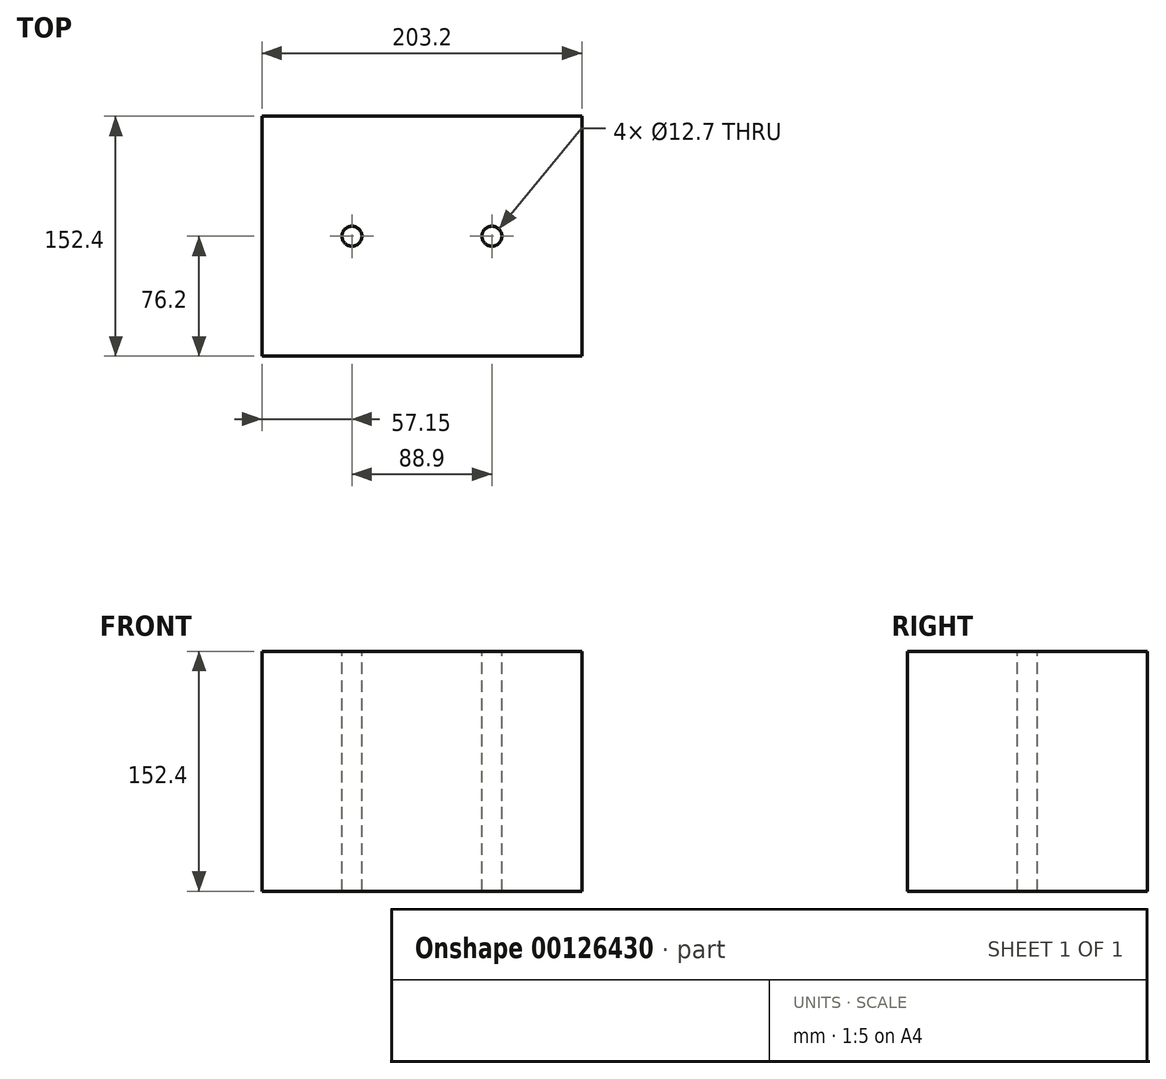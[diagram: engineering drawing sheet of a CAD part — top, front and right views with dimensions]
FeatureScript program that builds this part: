
annotation { "Feature Type Name" : "Feature", "Feature Type Description" : "" }
export const myFeature = defineFeature(function(context is Context, id is Id, definition is map)
    precondition{}
    {
        {
            var Q0;
            Q0=qCreatedBy(makeId("Top.planeOp"),FACE);
            var sketch = newSketch(context, id + "F0", { "sketchPlane" : qUnion([Q0])});
            skLineSegment(sketch, "E0.bottom", {"start": v(101.6, 76.2) * mm, "end": v(-101.6, 76.2) * mm});
            skLineSegment(sketch, "E0.top", {"start": v(101.6, -76.2) * mm, "end": v(-101.6, -76.2) * mm});
            skLineSegment(sketch, "E0.left", {"start": v(101.6, 76.2) * mm, "end": v(101.6, -76.2) * mm});
            skLineSegment(sketch, "E0.right", {"start": v(-101.6, 76.2) * mm, "end": v(-101.6, -76.2) * mm});
            skPoint(sketch, "E0.middle", {"position": v(0, 0) * mm});
            skSolve(sketch);
        }
        {
            var Q0;
            Q0 = qSketchRegion(id + "F0", true);
            extrude(context, id + "F1", {"entities" : qUnion([Q0]), "depth" : 152.4 * mm});
        }
        {
            var Q0;
            Q0=makeQuery(id+"F1.opExtrude","CAP_FACE",FACE,{"disambiguationData":[OSD([sQuery(id+"F0.wireOp",EDGE,"E0.bottom"),sQuery(id+"F0.wireOp",EDGE,"E0.top"),sQuery(id+"F0.wireOp",EDGE,"E0.left"),sQuery(id+"F0.wireOp",EDGE,"E0.right")])],"isStart":false});
            var sketch = newSketch(context, id + "F2", { "sketchPlane" : qUnion([Q0])});
            skLineSegment(sketch, "E1", {"start": v(0, 76.2) * mm, "end": v(0, -76.2) * mm, "construction": true});
            skLineSegment(sketch, "E2", {"start": v(-101.6, 0) * mm, "end": v(101.6, 0) * mm, "construction": true});
            skCircle(sketch, "E3", {"center": v(-44.45, 0) * mm, "radius": 6.35 * mm});
            skCircle(sketch, "E4", {"center": v(44.45, 0) * mm, "radius": 6.35 * mm});
            skSolve(sketch);
        }
        {
            var Q0;
            Q0 = qSketchRegion(id + "F2", true);
            extrude(context, id + "F3", {"entities" : qUnion([Q0]), "operationType" : NewBodyOperationType.REMOVE, "endBound" : BoundingType.THROUGH_ALL, "oppositeDirection" : true, "depth" : 25.4 * mm});
        }
    });
